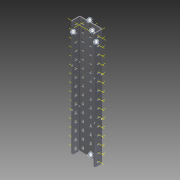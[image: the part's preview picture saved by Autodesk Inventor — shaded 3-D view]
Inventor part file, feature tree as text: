
AUTODESK INVENTOR PART (.ipt)
format: ipt  version: 2015 SP1 (Build 190203100, 203)  size: 2,034,688 bytes
history: native  units: in
note: dims shown in document units (in); Inventor stores cm internally (conversion verified against a paired STEP export)
features: other x81, pattern_linear x2, sheet_metal_op x1, extrude x1, imported_body x1, sketch x1
ambient origin geometry x8: Origin, YZ Plane, XZ Plane, XY Plane, X Axis, Y Axis, Z Axis, Center Point
bodies: Body1 (feature_tree)
feature tree (87):
  sheet_metal_op  "Fold1"
  other  "C-Channel"
  extrude  "length cut"  Depth=1.1811in
  other  "Work Point1"
  other  "Work Point2"
  other  "Work Point3"
  other  "top axis"
  other  "front axis"
  other  "back axis"
  pattern_linear  "top axes"  Count1=15  [1 undecoded]
  pattern_linear  "horiz axes"  Spacing1=0.5in  [1 undecoded]
  other  "Left Plane"
  other  "Right Plane"
  imported_body  "Base1"
  sketch  "Sketch1"  dims[d1=0.0in d2=1.1811in d4=0.5in d5=5.9055in d7=0.5in d8=5.9055in d10=0.5in d12=-7.5in d17=0.0in d18=0.0in d19=0.0in d20=0.0in d21=0.0in]
  other  "Work Axis4"
  other  "Work Axis5"
  other  "Work Axis6"
  other  "Work Axis7"
  other  "Work Axis8"
  other  "Work Axis9"
  other  "Work Axis10"
  other  "Work Axis11"
  other  "Work Axis12"
  other  "Work Axis13"
  other  "Work Axis14"
  other  "Work Axis15"
  other  "Work Axis16"
  other  "Work Axis17"
  other  "Work Axis18"
  other  "Work Axis19"
  other  "Work Axis20"
  other  "Work Axis21"
  other  "Work Axis22"
  other  "Work Axis23"
  other  "Work Axis24"
  other  "Work Axis25"
  other  "Work Axis26"
  other  "Work Axis27"
  other  "Work Axis28"
  other  "Work Axis29"
  other  "Work Axis30"
  other  "Work Axis31"
  other  "Work Axis32"
  other  "Work Axis33"
  other  "Work Axis34"
  other  "Work Axis35"
  other  "Work Axis36"
  other  "Work Axis37"
  other  "Work Axis38"
  other  "Work Axis39"
  other  "Work Axis40"
  other  "Work Axis41"
  other  "Work Axis42"
  other  "Work Axis43"
  other  "Work Axis44"
  other  "Work Axis45"
  other  "Work Axis46"
  other  "Work Axis47"
  other  "Work Axis48"
  other  "Work Axis49"
  other  "Work Axis50"
  other  "Work Axis51"
  other  "Work Axis52"
  other  "Work Axis53"
  other  "Work Axis54"
  other  "Work Axis55"
  other  "Work Axis56"
  other  "Work Axis57"
  other  "Work Axis58"
  other  "Work Axis59"
  other  "Work Axis60"
  other  "Work Axis61"
  other  "Work Axis62"
  other  "Work Axis63"
  other  "Work Axis64"
  other  "Work Axis65"
  other  "Work Axis66"
  other  "Work Axis67"
  other  "Work Axis68"
  other  "Work Axis69"
  other  "Work Axis70"
  other  "Work Axis71"
  other  "Work Axis72"
  other  "Work Axis73"
  other  "Work Axis74"
  other  "Work Axis75"
note: 2 required parameter values undecoded (feature->parameter linkage not recoverable at this tier; creation-order binding heuristic only, values carry confidence <= 0.55)
